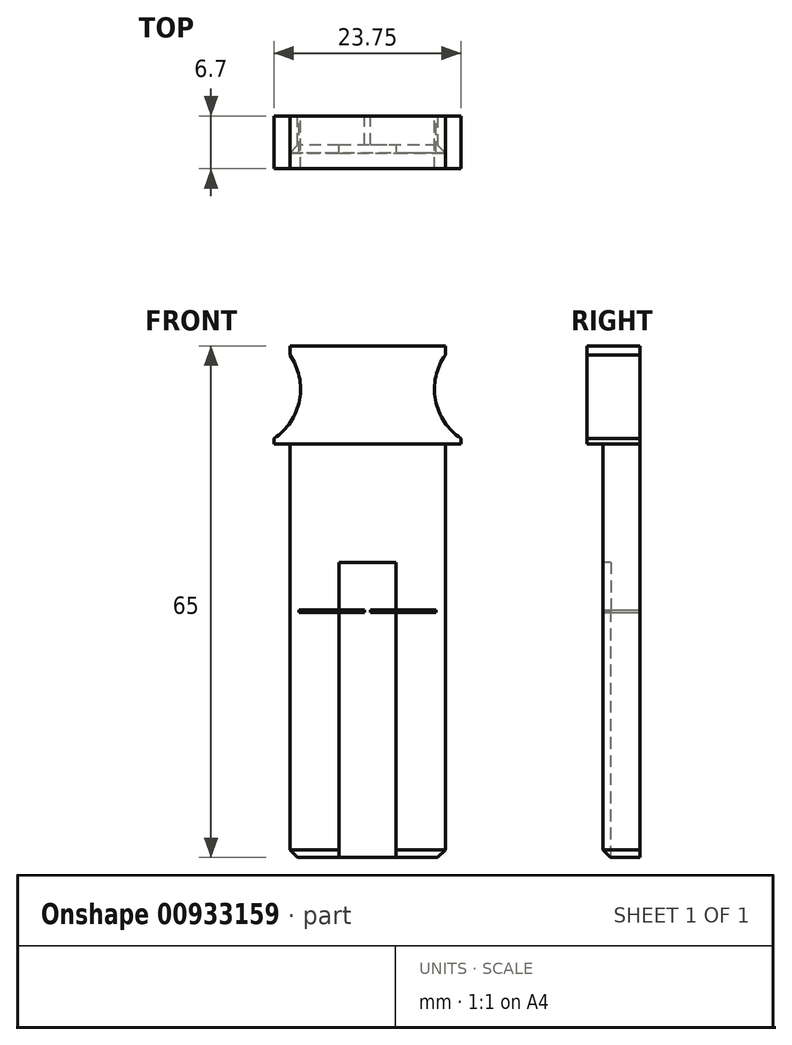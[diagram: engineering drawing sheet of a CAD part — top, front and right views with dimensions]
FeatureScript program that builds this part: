
annotation { "Feature Type Name" : "Feature", "Feature Type Description" : "" }
export const myFeature = defineFeature(function(context is Context, id is Id, definition is map)
    precondition{}
    {
        {
            var Q0;
            Q0=qCreatedBy(makeId("Front.planeOp"),FACE);
            var sketch = newSketch(context, id + "F0", { "sketchPlane" : qUnion([Q0])});
            skLineSegment(sketch, "E0.bottom", {"start": v(0, 0) * mm, "end": v(19.75, 0) * mm});
            skLineSegment(sketch, "E0.top", {"start": v(0, 65) * mm, "end": v(19.75, 65) * mm});
            skLineSegment(sketch, "E0.left", {"start": v(0, 0) * mm, "end": v(0, 65) * mm});
            skLineSegment(sketch, "E0.right", {"start": v(19.75, 0) * mm, "end": v(19.75, 65) * mm});
            skLineSegment(sketch, "E1", {"start": v(9.87, 65) * mm, "end": v(9.87, 0) * mm, "construction": true});
            skPoint(sketch, "E2", {"position": v(9.87, 38.5) * mm});
            skLineSegment(sketch, "E3", {"start": v(-7.67, 31.3) * mm, "end": v(34.9, 31.3) * mm, "construction": true});
            skLineSegment(sketch, "E4", {"start": v(0, 31.15) * mm, "end": v(0, 31.45) * mm});
            skCircle(sketch, "E5", {"center": v(25.88, 59.5) * mm, "radius": 7.5 * mm});
            skCircle(sketch, "E6.MirrorC", {"center": v(-6.13, 59.5) * mm, "radius": 7.5 * mm});
            skLineSegment(sketch, "E7.bottom", {"start": v(0, 31.45) * mm, "end": v(9.47, 31.45) * mm});
            skLineSegment(sketch, "E7.top", {"start": v(0, 31.45) * mm, "end": v(9.47, 31.45) * mm});
            skLineSegment(sketch, "E7.left", {"start": v(0, 31.45) * mm, "end": v(0, 31.45) * mm});
            skLineSegment(sketch, "E7.right", {"start": v(9.47, 31.45) * mm, "end": v(9.47, 31.45) * mm});
            skLineSegment(sketch, "E8", {"start": v(9.47, 31.45) * mm, "end": v(9.47, 31.15) * mm});
            skLineSegment(sketch, "E9", {"start": v(9.47, 31.15) * mm, "end": v(0, 31.15) * mm});
            skLineSegment(sketch, "E10", {"start": v(0, 31.45) * mm, "end": v(0, 31.15) * mm});
            skLineSegment(sketch, "E11.MirrorCS", {"start": v(19.75, 31.45) * mm, "end": v(10.28, 31.45) * mm});
            skLineSegment(sketch, "E12.MirrorCS", {"start": v(10.27, 31.45) * mm, "end": v(10.27, 31.15) * mm});
            skLineSegment(sketch, "E13.MirrorCS", {"start": v(10.28, 31.15) * mm, "end": v(19.75, 31.15) * mm});
            skLineSegment(sketch, "E14.MirrorCS", {"start": v(19.75, 31.45) * mm, "end": v(19.75, 31.15) * mm});
            skLineSegment(sketch, "E15.bottom", {"start": v(0, 52.5) * mm, "end": v(-2, 52.5) * mm});
            skLineSegment(sketch, "E15.top", {"start": v(0, 65.03) * mm, "end": v(-2, 65.03) * mm});
            skLineSegment(sketch, "E15.left", {"start": v(0, 52.5) * mm, "end": v(0, 65.03) * mm});
            skLineSegment(sketch, "E15.right", {"start": v(-2, 52.5) * mm, "end": v(-2, 65.03) * mm});
            skLineSegment(sketch, "E16.MirrorCS", {"start": v(19.75, 65.03) * mm, "end": v(21.75, 65.03) * mm});
            skLineSegment(sketch, "E17.MirrorCS", {"start": v(21.75, 52.5) * mm, "end": v(21.75, 65.03) * mm});
            skLineSegment(sketch, "E18.MirrorCS", {"start": v(19.75, 52.5) * mm, "end": v(21.75, 52.5) * mm});
            skLineSegment(sketch, "E19", {"start": v(1.2, 31.45) * mm, "end": v(1.2, 31.15) * mm});
            skLineSegment(sketch, "E20.MirrorCS", {"start": v(18.55, 31.45) * mm, "end": v(18.55, 31.15) * mm});
            skSolve(sketch);
        }
        {
            var Q0;
            {var subQ4=sQuery(id+"F0.wireOp",EDGE,"E0.bottom");Q0=makeQuery(id+"F0.imprint","IMPRINT",FACE,{"disambiguationData":[TD([[makeQuery(id+"F0.imprint","IMPRINT",EDGE,{"derivedFrom":subQ4}),1.0]])]});}
            var Q1;
            {var subQ0=sQuery(id+"F0.wireOp",EDGE,"E15.bottom");Q1=makeQuery(id+"F0.imprint","IMPRINT",FACE,{"disambiguationData":[TD([[makeQuery(id+"F0.imprint","IMPRINT",EDGE,{"derivedFrom":subQ0}),-1.0]])]});}
            var Q2;
            {var subQ0=sQuery(id+"F0.wireOp",EDGE,"E18.MirrorCS");Q2=makeQuery(id+"F0.imprint","IMPRINT",FACE,{"disambiguationData":[TD([[makeQuery(id+"F0.imprint","IMPRINT",EDGE,{"derivedFrom":subQ0}),1.0]])]});}
            var Q3;
            {var subQ5=sQuery(id+"F0.wireOp",EDGE,"E19");Q3=makeQuery(id+"F0.imprint","IMPRINT",FACE,{"disambiguationData":[TD([[makeQuery(id+"F0.imprint","IMPRINT",EDGE,{"derivedFrom":subQ5}),-1.0]])]});}
            var Q4;
            {var subQ5=sQuery(id+"F0.wireOp",EDGE,"E20.MirrorCS");Q4=makeQuery(id+"F0.imprint","IMPRINT",FACE,{"disambiguationData":[TD([[makeQuery(id+"F0.imprint","IMPRINT",EDGE,{"derivedFrom":subQ5}),1.0]])]});}
            extrude(context, id + "F1", {"entities" : qUnion([Q0, Q1, Q2, Q3, Q4]), "depth" : 4.7 * mm, "offsetDistance" : 25 * mm});
        }
        {
            var Q0;
            Q0=makeQuery(id+"F1.opExtrude","CAP_FACE",FACE,{"disambiguationData":[OSD([sQuery(id+"F0.wireOp",EDGE,"E0.bottom"),sQuery(id+"F0.wireOp",EDGE,"E0.top"),sQuery(id+"F0.wireOp",EDGE,"E0.left"),sQuery(id+"F0.wireOp",EDGE,"E0.right"),sQuery(id+"F0.wireOp",EDGE,"E5"),sQuery(id+"F0.wireOp",EDGE,"E6.MirrorC"),sQuery(id+"F0.wireOp",EDGE,"E7.bottom"),sQuery(id+"F0.wireOp",EDGE,"E8"),sQuery(id+"F0.wireOp",EDGE,"E9"),sQuery(id+"F0.wireOp",EDGE,"E11.MirrorCS"),sQuery(id+"F0.wireOp",EDGE,"E12.MirrorCS"),sQuery(id+"F0.wireOp",EDGE,"E13.MirrorCS"),sQuery(id+"F0.wireOp",EDGE,"E15.bottom"),sQuery(id+"F0.wireOp",EDGE,"E15.right"),sQuery(id+"F0.wireOp",EDGE,"E17.MirrorCS"),sQuery(id+"F0.wireOp",EDGE,"E18.MirrorCS"),sQuery(id+"F0.wireOp",EDGE,"E19"),sQuery(id+"F0.wireOp",EDGE,"E20.MirrorCS")])],"isStart":false});
            var sketch = newSketch(context, id + "F2", { "sketchPlane" : qUnion([Q0])});
            skLineSegment(sketch, "E21", {"start": v(6.27, 37.5) * mm, "end": v(13.47, 37.5) * mm});
            skLineSegment(sketch, "E22", {"start": v(13.47, 37.5) * mm, "end": v(13.47, 2.2) * mm});
            skLineSegment(sketch, "E23", {"start": v(13.47, 2.2) * mm, "end": v(13.47, 2.2) * mm});
            skLineSegment(sketch, "E24", {"start": v(13.47, 2.2) * mm, "end": v(13.47, 0) * mm});
            skLineSegment(sketch, "E25", {"start": v(13.47, 0) * mm, "end": v(6.27, 0) * mm});
            skLineSegment(sketch, "E26", {"start": v(6.27, 0) * mm, "end": v(6.27, 2.2) * mm});
            skLineSegment(sketch, "E27", {"start": v(6.27, 2.2) * mm, "end": v(6.27, 2.2) * mm});
            skLineSegment(sketch, "E28", {"start": v(6.27, 2.2) * mm, "end": v(6.27, 37.5) * mm});
            skLineSegment(sketch, "E29", {"start": v(9.87, 65) * mm, "end": v(9.87, 0) * mm, "construction": true});
            skSolve(sketch);
        }
        {
            var Q0;
            Q0=qSketchRegion(id+"F2",true);
            extrude(context, id + "F3", {"entities" : qUnion([Q0]), "operationType" : NewBodyOperationType.REMOVE, "oppositeDirection" : true, "depth" : 1.05 * mm, "offsetDistance" : 25 * mm});
        }
        {
            var Q0;
            {var subQ0=sQuery(id+"F0.wireOp",EDGE,"E0.right");Q0=makeQuery(id+"F1.opExtrude","SWEPT_FACE",FACE,{"disambiguationData":[OSD([subQ0]),TDD([makeQuery(id+"F0.imprint","IMPRINT",EDGE,{"disambiguationData":[TD([[makeQuery(id+"F0.imprint","INTERSECT",VERTEX,{"derivedFrom":[sQuery(id+"F0.wireOp",EDGE,"E0.top"),subQ0]}),1.0]])],"derivedFrom":subQ0})])]});}
            var sketch = newSketch(context, id + "F4", { "sketchPlane" : qUnion([Q0])});
            skLineSegment(sketch, "E30", {"start": v(-15.64, 31.3) * mm, "end": v(17.74, 31.3) * mm, "construction": true});
            skLineSegment(sketch, "E31", {"start": v(-1, 31.3) * mm, "end": v(0, 32.3) * mm});
            skLineSegment(sketch, "E32", {"start": v(0, 32.3) * mm, "end": v(0, 30.3) * mm});
            skLineSegment(sketch, "E33", {"start": v(0, 30.3) * mm, "end": v(-1, 31.3) * mm});
            skSolve(sketch);
        }
        {
            var Q0;
            Q0=makeQuery(id+"F1.opExtrude","CAP_FACE",FACE,{"disambiguationData":[OSD([sQuery(id+"F0.wireOp",EDGE,"E0.bottom"),sQuery(id+"F0.wireOp",EDGE,"E0.top"),sQuery(id+"F0.wireOp",EDGE,"E0.left"),sQuery(id+"F0.wireOp",EDGE,"E0.right"),sQuery(id+"F0.wireOp",EDGE,"E5"),sQuery(id+"F0.wireOp",EDGE,"E6.MirrorC"),sQuery(id+"F0.wireOp",EDGE,"E7.bottom"),sQuery(id+"F0.wireOp",EDGE,"E8"),sQuery(id+"F0.wireOp",EDGE,"E9"),sQuery(id+"F0.wireOp",EDGE,"E11.MirrorCS"),sQuery(id+"F0.wireOp",EDGE,"E12.MirrorCS"),sQuery(id+"F0.wireOp",EDGE,"E13.MirrorCS"),sQuery(id+"F0.wireOp",EDGE,"E15.bottom"),sQuery(id+"F0.wireOp",EDGE,"E15.right"),sQuery(id+"F0.wireOp",EDGE,"E17.MirrorCS"),sQuery(id+"F0.wireOp",EDGE,"E18.MirrorCS"),sQuery(id+"F0.wireOp",EDGE,"E19"),sQuery(id+"F0.wireOp",EDGE,"E20.MirrorCS")])],"isStart":false});
            var sketch = newSketch(context, id + "F5", { "sketchPlane" : qUnion([Q0])});
            skLineSegment(sketch, "E34", {"start": v(0, 52.5) * mm, "end": v(19.75, 52.5) * mm});
            skSolve(sketch);
        }
        {
            var Q0;
            Q0=makeQuery(id+"F5.imprint","IMPRINT",FACE,{"disambiguationData":[TD([[makeQuery(id+"F5.imprint","IMPRINT",EDGE,{"derivedFrom":sQuery(id+"F5.wireOp",EDGE,"E34")}),1.0]])]});
            extrude(context, id + "F6", {"entities" : qUnion([Q0]), "operationType" : NewBodyOperationType.ADD, "depth" : 2 * mm, "offsetDistance" : 25 * mm});
        }
        {
            var Q0;
            Q0=makeQuery(id+"F1.opExtrude","SWEPT_EDGE",EDGE,{"disambiguationData":[OSD([sQuery(id+"F0.wireOp",EDGE,"E0.bottom"),sQuery(id+"F0.wireOp",EDGE,"E0.left")])]});
            var Q1;
            Q1=makeQuery(id+"F1.opExtrude","SWEPT_EDGE",EDGE,{"disambiguationData":[OSD([sQuery(id+"F0.wireOp",EDGE,"E0.bottom"),sQuery(id+"F0.wireOp",EDGE,"E0.right")])]});
            var Q2;
            {var subQ0=sQuery(id+"F0.wireOp",EDGE,"E0.bottom");Q2=makeQuery(id+"F3.boolean.opBoolean","SPLIT",EDGE,{"disambiguationData":[TD([makeQuery(id+"F3.opExtrude","SWEPT_FACE",FACE,{"disambiguationData":[OSD([sQuery(id+"F2.wireOp",EDGE,"E26"),sQuery(id+"F2.wireOp",EDGE,"E28")])]})])],"derivedFrom":makeQuery(id+"F1.opExtrude","CAP_EDGE",EDGE,{"disambiguationData":[OSD([subQ0])],"isStart":false})});}
            var Q3;
            {var subQ0=sQuery(id+"F0.wireOp",EDGE,"E0.bottom");Q3=makeQuery(id+"F3.boolean.opBoolean","SPLIT",EDGE,{"disambiguationData":[TD([makeQuery(id+"F3.opExtrude","SWEPT_FACE",FACE,{"disambiguationData":[OSD([sQuery(id+"F2.wireOp",EDGE,"E22"),sQuery(id+"F2.wireOp",EDGE,"E24")])]})])],"derivedFrom":makeQuery(id+"F1.opExtrude","CAP_EDGE",EDGE,{"disambiguationData":[OSD([subQ0])],"isStart":false})});}
            var Q4;
            Q4=makeQuery(id+"F3.boolean.opBoolean","COPY",EDGE,{"derivedFrom":makeQuery(id+"F3.opExtrude","CAP_EDGE",EDGE,{"disambiguationData":[OSD([sQuery(id+"F2.wireOp",EDGE,"E25")])],"isStart":false})});
            chamfer(context, id + "F7", {"entities" : qUnion([Q0, Q1, Q2, Q3, Q4]), "width" : 1 * mm, "tangentPropagation" : true});
        }
    });
